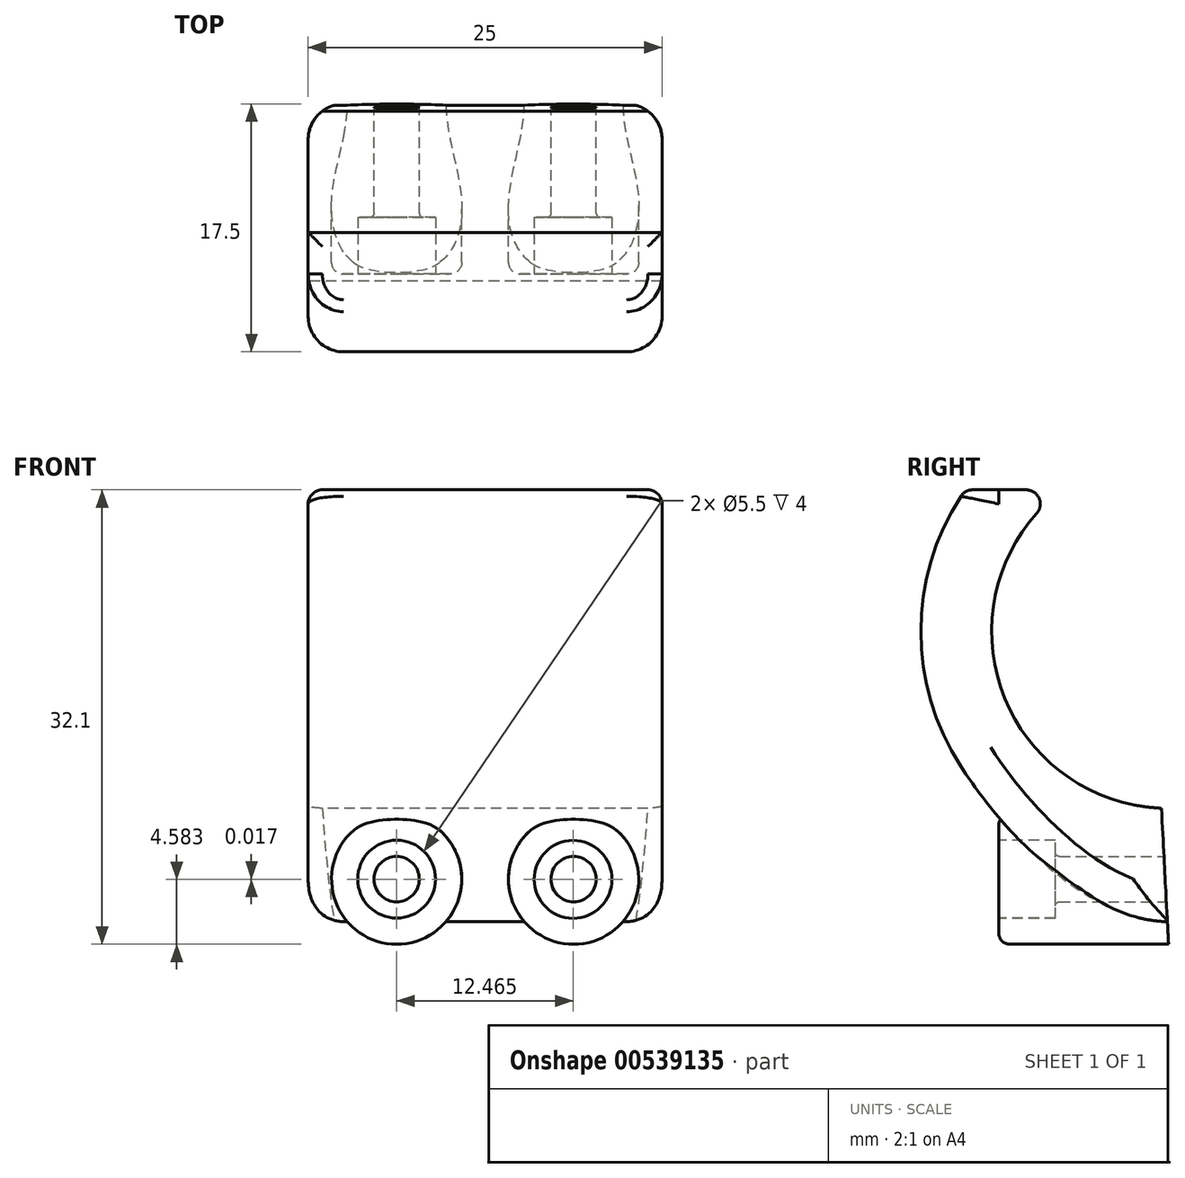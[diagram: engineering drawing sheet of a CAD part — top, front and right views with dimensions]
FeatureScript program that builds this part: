
annotation { "Feature Type Name" : "Feature", "Feature Type Description" : "" }
export const myFeature = defineFeature(function(context is Context, id is Id, definition is map)
    precondition{}
    {
        {
            var Q0;
            Q0=qCreatedBy(makeId("Right.planeOp"),FACE);
            var sketch = newSketch(context, id + "F0", { "sketchPlane" : qUnion([Q0])});
            skArc(sketch, "E0", {"start": v(-10.36, 7) * mm, "mid": v(-11.04, -5.86) * mm, "end": v(0, -12.5) * mm});
            skArc(sketch, "E1.0", {"start": v(-16.04, 7) * mm, "mid": v(-17.44, -1.45) * mm, "end": v(-14.67, -9.55) * mm});
            skLineSegment(sketch, "E2", {"start": v(0, 0) * mm, "end": v(0, 7) * mm, "construction": true});
            skLineSegment(sketch, "E3", {"start": v(0, 0) * mm, "end": v(0, -17.5) * mm, "construction": true});
            skPoint(sketch, "E4.start.orphan", {"position": v(0, -24.5) * mm});
            skLineSegment(sketch, "E5", {"start": v(0, -12.5) * mm, "end": v(0, -17.5) * mm});
            skLineSegment(sketch, "E6", {"start": v(0, -17.5) * mm, "end": v(0, -20.5) * mm});
            skFitSpline(sketch, "E7", {"points": [v(-14.67, -9.55) * mm, v(0, -20.5) * mm], "startDerivative": vector(11.8, -18.12) * mm, "endDerivative": vector(14.84, 0) * mm});
            skLineSegment(sketch, "E8", {"start": v(0, -20.5) * mm, "end": v(26.15, -20.5) * mm, "construction": true});
            skArc(sketch, "E9", {"start": v(-8.67, 9) * mm, "mid": v(-11.6, -4.68) * mm, "end": v(0, -12.5) * mm});
            skArc(sketch, "E10", {"start": v(-15, 9) * mm, "mid": v(-17.5, -0.32) * mm, "end": v(-14.67, -9.55) * mm});
            skLineSegment(sketch, "E11.0", {"start": v(-7.58, 10) * mm, "end": v(-14.36, 10) * mm});
            skArc(sketch, "E12", {"start": v(-7.58, 10) * mm, "mid": v(-8.14, 9.52) * mm, "end": v(-8.67, 9) * mm});
            skArc(sketch, "E13", {"start": v(-14.36, 10) * mm, "mid": v(-17.5, 0.27) * mm, "end": v(-14.67, -9.55) * mm});
            skSolve(sketch);
        }
        {
            var Q0;
            {var subQ1=sQuery(id+"F0.wireOp",EDGE,"E5");Q0=makeQuery(id+"F0.imprint","IMPRINT",FACE,{"disambiguationData":[TD([[makeQuery(id+"F0.imprint","IMPRINT",EDGE,{"derivedFrom":subQ1}),-1.0]])]});}
            extrude(context, id + "F1", {"entities" : qUnion([Q0]), "depth" : 25 * mm, "offsetDistance" : 25 * mm});
        }
        {
            var Q0;
            Q0=qCreatedBy(makeId("Front.planeOp"),FACE);
            var sketch = newSketch(context, id + "F2", { "sketchPlane" : qUnion([Q0])});
            skLineSegment(sketch, "E14", {"start": v(25, -17.5) * mm, "end": v(0, -17.5) * mm, "construction": true});
            skLineSegment(sketch, "E15", {"start": v(12.5, -17.5) * mm, "end": v(0, -17.5) * mm, "construction": true});
            skLineSegment(sketch, "E16", {"start": v(12.5, -17.5) * mm, "end": v(25, -17.5) * mm, "construction": true});
            skCircle(sketch, "E17", {"center": v(18.75, -17.5) * mm, "radius": 1.6 * mm});
            skCircle(sketch, "E18", {"center": v(6.25, -17.5) * mm, "radius": 1.6 * mm});
            skCircle(sketch, "E19.0", {"center": v(6.25, -17.5) * mm, "radius": 4.6 * mm});
            skCircle(sketch, "E20.0", {"center": v(18.75, -17.5) * mm, "radius": 4.6 * mm});
            skSolve(sketch);
        }
        {
            var Q0;
            Q0=makeQuery(id+"F2.imprint","IMPRINT",FACE,{"disambiguationData":[TD([[makeQuery(id+"F2.imprint","IMPRINT",EDGE,{"derivedFrom":sQuery(id+"F2.wireOp",EDGE,"E18")}),-1.0]])]});
            var Q1;
            Q1=makeQuery(id+"F2.imprint","IMPRINT",FACE,{"disambiguationData":[TD([[makeQuery(id+"F2.imprint","IMPRINT",EDGE,{"derivedFrom":sQuery(id+"F2.wireOp",EDGE,"E17")}),-1.0]])]});
            extrude(context, id + "F3", {"entities" : qUnion([Q0, Q1]), "operationType" : NewBodyOperationType.ADD, "depth" : 12 * mm, "offsetDistance" : 25 * mm});
        }
        {
            var Q0;
            Q0=makeQuery(id+"F2.imprint","IMPRINT",FACE,{"disambiguationData":[TD([[makeQuery(id+"F2.imprint","IMPRINT",EDGE,{"derivedFrom":sQuery(id+"F2.wireOp",EDGE,"E18")}),1.0]])]});
            var Q1;
            Q1=makeQuery(id+"F2.imprint","IMPRINT",FACE,{"disambiguationData":[TD([[makeQuery(id+"F2.imprint","IMPRINT",EDGE,{"derivedFrom":sQuery(id+"F2.wireOp",EDGE,"E17")}),1.0]])]});
            extrude(context, id + "F4", {"entities" : qUnion([Q0, Q1]), "operationType" : NewBodyOperationType.REMOVE, "endBound" : BoundingType.SYMMETRIC, "oppositeDirection" : true, "depth" : 100 * mm, "offsetDistance" : 25 * mm});
        }
        {
            var Q0;
            Q0=makeQuery(id+"F1.opExtrude","CAP_EDGE",EDGE,{"disambiguationData":[OSD([sQuery(id+"F0.wireOp",EDGE,"E1.0")])],"isStart":false});
            var Q1;
            Q1=makeQuery(id+"F1.opExtrude","CAP_EDGE",EDGE,{"disambiguationData":[OSD([sQuery(id+"F0.wireOp",EDGE,"E1.0")])],"isStart":true});
            var Q2;
            Q2=makeQuery(id+"F1.opExtrude","CAP_EDGE",EDGE,{"disambiguationData":[OSD([sQuery(id+"F0.wireOp",EDGE,"E5"),sQuery(id+"F0.wireOp",EDGE,"E6")])],"isStart":false});
            var Q3;
            Q3=makeQuery(id+"F1.opExtrude","CAP_EDGE",EDGE,{"disambiguationData":[OSD([sQuery(id+"F0.wireOp",EDGE,"E5"),sQuery(id+"F0.wireOp",EDGE,"E6")])],"isStart":true});
            var Q4;
            Q4=makeQuery(id+"F1.opExtrude","CAP_EDGE",EDGE,{"disambiguationData":[OSD([sQuery(id+"F0.wireOp",EDGE,"E10")])],"isStart":false});
            var Q5;
            Q5=makeQuery(id+"F1.opExtrude","CAP_EDGE",EDGE,{"disambiguationData":[OSD([sQuery(id+"F0.wireOp",EDGE,"E10")])],"isStart":true});
            var Q6;
            Q6=makeQuery(id+"F1.opExtrude","CAP_EDGE",EDGE,{"disambiguationData":[OSD([sQuery(id+"F0.wireOp",EDGE,"E13")])],"isStart":false});
            var Q7;
            Q7=makeQuery(id+"F1.opExtrude","CAP_EDGE",EDGE,{"disambiguationData":[OSD([sQuery(id+"F0.wireOp",EDGE,"E13")])],"isStart":true});
            fillet(context, id + "F5", {"entities" : qUnion([Q0, Q1, Q2, Q3, Q4, Q5, Q6, Q7]), "radius" : 2.5 * mm, "tangentPropagation" : true, "allowEdgeOverflow" : false});
        }
        {
            var Q0;
            Q0=makeQuery(id+"F3.opExtrude","CAP_FACE",FACE,{"disambiguationData":[OSD([sQuery(id+"F2.wireOp",EDGE,"E18"),sQuery(id+"F2.wireOp",EDGE,"E19.0")])],"isStart":false});
            var sketch = newSketch(context, id + "F6", { "sketchPlane" : qUnion([Q0])});
            skCircle(sketch, "E21.cCircle", {"center": v(6.25, -17.5) * mm, "radius": 2.75 * mm});
            skCircle(sketch, "E22.cCircle", {"center": v(18.71, -17.52) * mm, "radius": 2.75 * mm});
            skSolve(sketch);
        }
        {
            var Q0;
            Q0 = qSketchRegion(id + "F6", true);
            extrude(context, id + "F7", {"entities" : qUnion([Q0]), "operationType" : NewBodyOperationType.REMOVE, "oppositeDirection" : true, "depth" : 4 * mm, "offsetDistance" : 25 * mm});
        }
        {
            var Q0;
            Q0=qCreatedBy(makeId("Right.planeOp"),FACE);
            var sketch = newSketch(context, id + "F8", { "sketchPlane" : qUnion([Q0])});
            skLineSegment(sketch, "E23.0.4", {"start": v(0, -20.61) * mm, "end": v(0, -12.5) * mm});
            skLineSegment(sketch, "E24", {"start": v(0, -12.5) * mm, "end": v(-0.5, -12.5) * mm});
            skLineSegment(sketch, "E25", {"start": v(0, -22.1) * mm, "end": v(-14, -22.1) * mm, "construction": true});
            skLineSegment(sketch, "E26", {"start": v(0, -22.1) * mm, "end": v(-0.5, -12.5) * mm});
            skLineSegment(sketch, "E27", {"start": v(0, -12.5) * mm, "end": v(0, -22.1) * mm});
            skSolve(sketch);
        }
        {
            var Q0;
            {var subQ0=sQuery(id+"F8.wireOp",EDGE,"E24");Q0=makeQuery(id+"F8.imprint","IMPRINT",FACE,{"disambiguationData":[TD([[makeQuery(id+"F8.imprint","IMPRINT",EDGE,{"derivedFrom":subQ0}),1.0]])]});}
            extrude(context, id + "F9", {"entities" : qUnion([Q0]), "operationType" : NewBodyOperationType.REMOVE, "depth" : 25 * mm, "offsetDistance" : 25 * mm});
        }
        {
            var Q0;
            Q0=makeQuery(id+"F1.opExtrude","SWEPT_FACE",FACE,{"disambiguationData":[OSD([sQuery(id+"F0.wireOp",EDGE,"E11.0")])]});
            fillet(context, id + "F10", {"entities" : qUnion([Q0]), "radius" : 1 * mm, "tangentPropagation" : true, "allowEdgeOverflow" : false});
        }
        {
            var Q0;
            Q0=makeQuery(id+"F7.boolean.opBoolean","COPY",EDGE,{"derivedFrom":makeQuery(id+"F7.opExtrude","CAP_EDGE",EDGE,{"disambiguationData":[OSD([sQuery(id+"F6.wireOp",EDGE,"E21.cCircle")])],"isStart":true})});
            var Q1;
            Q1=makeQuery(id+"F7.boolean.opBoolean","COPY",EDGE,{"derivedFrom":makeQuery(id+"F7.opExtrude","CAP_EDGE",EDGE,{"disambiguationData":[OSD([sQuery(id+"F6.wireOp",EDGE,"E22.cCircle")])],"isStart":true})});
            var Q2;
            Q2=makeQuery(id+"F3.opExtrude","CAP_EDGE",EDGE,{"disambiguationData":[OSD([sQuery(id+"F2.wireOp",EDGE,"E19.0")])],"isStart":false});
            var Q3;
            Q3=makeQuery(id+"F3.opExtrude","CAP_EDGE",EDGE,{"disambiguationData":[OSD([sQuery(id+"F2.wireOp",EDGE,"E20.0")])],"isStart":false});
            fillet(context, id + "F11", {"entities" : qUnion([Q0, Q1, Q2, Q3]), "radius" : .8 * mm, "tangentPropagation" : true, "allowEdgeOverflow" : false});
        }
        {
            var Q0;
            {var subQ0=sQuery(id+"F2.wireOp",EDGE,"E18");Q0=makeQuery(id+"F7.boolean.opBoolean","INTERSECT",EDGE,{"derivedFrom":[makeQuery(id+"F4.boolean.opBoolean","MERGE",FACE,{"derivedFrom":[makeQuery(id+"F3.opExtrude","SWEPT_FACE",FACE,{"disambiguationData":[OSD([subQ0])]}),makeQuery(id+"F4.opExtrude","SWEPT_FACE",FACE,{"disambiguationData":[OSD([subQ0])]})]}),makeQuery(id+"F7.opExtrude","CAP_FACE",FACE,{"disambiguationData":[OSD([sQuery(id+"F6.wireOp",EDGE,"E21.cCircle")])],"isStart":false})]});}
            var Q1;
            {var subQ0=sQuery(id+"F2.wireOp",EDGE,"E17");Q1=makeQuery(id+"F7.boolean.opBoolean","INTERSECT",EDGE,{"derivedFrom":[makeQuery(id+"F4.boolean.opBoolean","MERGE",FACE,{"derivedFrom":[makeQuery(id+"F3.opExtrude","SWEPT_FACE",FACE,{"disambiguationData":[OSD([subQ0])]}),makeQuery(id+"F4.opExtrude","SWEPT_FACE",FACE,{"disambiguationData":[OSD([subQ0])]})]}),makeQuery(id+"F7.opExtrude","CAP_FACE",FACE,{"disambiguationData":[OSD([sQuery(id+"F6.wireOp",EDGE,"E22.cCircle")])],"isStart":false})]});}
            fillet(context, id + "F12", {"entities" : qUnion([Q0, Q1]), "radius" : 0.3 * mm, "tangentPropagation" : true, "allowEdgeOverflow" : false});
        }
    });
